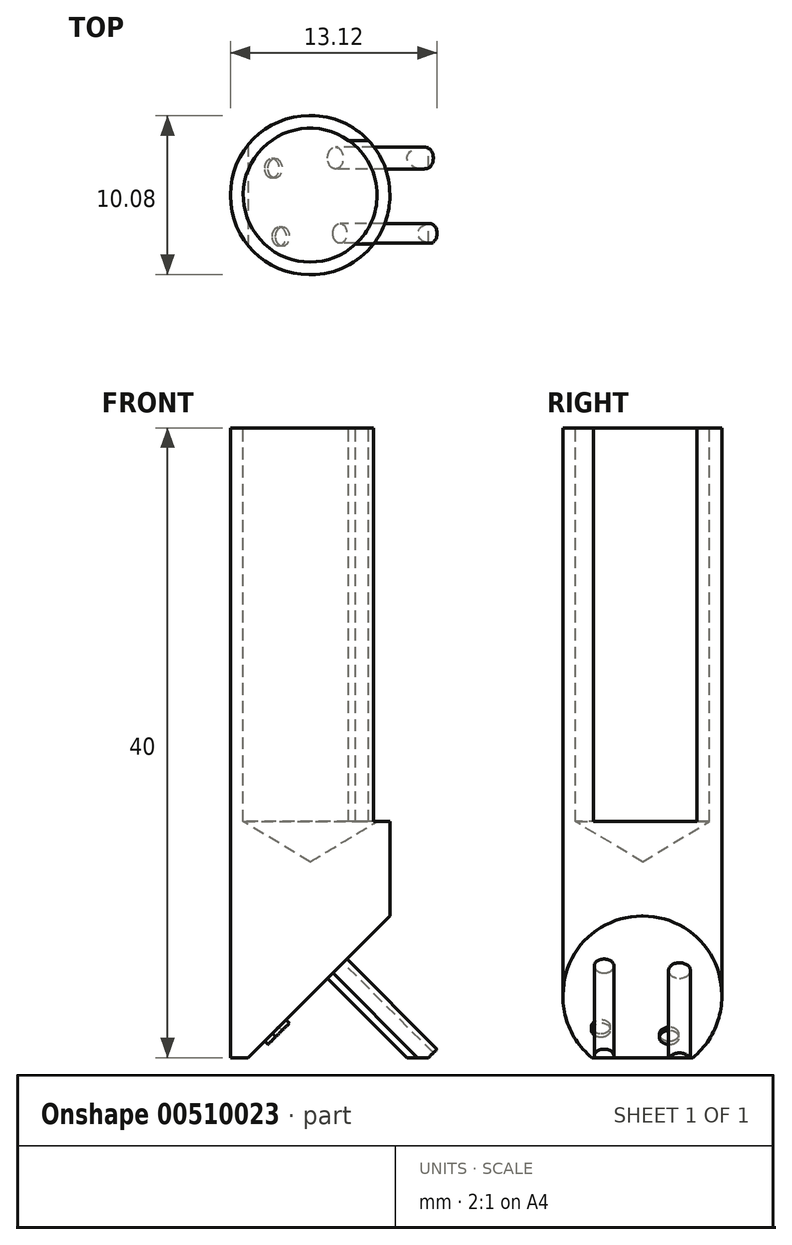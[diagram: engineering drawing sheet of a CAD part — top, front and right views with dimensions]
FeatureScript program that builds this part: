
annotation { "Feature Type Name" : "Feature", "Feature Type Description" : "" }
export const myFeature = defineFeature(function(context is Context, id is Id, definition is map)
    precondition{}
    {
        {
            var Q0;
            Q0=qCreatedBy(makeId("Top.planeOp"),FACE);
            var sketch = newSketch(context, id + "F0", { "sketchPlane" : qUnion([Q0])});
            skLineSegment(sketch, "E0.bottom", {"start": v(-5.06, -5.04) * mm, "end": v(5.06, -5.04) * mm});
            skLineSegment(sketch, "E0.top", {"start": v(-5.06, 5.04) * mm, "end": v(5.06, 5.04) * mm});
            skLineSegment(sketch, "E0.left", {"start": v(-5.06, -5.04) * mm, "end": v(-5.06, 5.04) * mm});
            skLineSegment(sketch, "E0.right", {"start": v(5.06, -5.04) * mm, "end": v(5.06, 5.04) * mm});
            skPoint(sketch, "E0.middle", {"position": v(0, 0) * mm});
            skSolve(sketch);
        }
        {
            var Q0;
            Q0=makeQuery(id+"F0.imprint","IMPRINT",FACE,{"disambiguationData":[TD([[makeQuery(id+"F0.imprint","IMPRINT",EDGE,{"derivedFrom":sQuery(id+"F0.wireOp",EDGE,"E0.bottom")}),1.0]])]});
            extrude(context, id + "F1", {"entities" : qUnion([Q0]), "depth" : 40 * mm});
        }
        {
            var Q0;
            Q0=makeQuery(id+"F1.opExtrude","CAP_FACE",FACE,{"disambiguationData":[OSD([sQuery(id+"F0.wireOp",EDGE,"E0.bottom"),sQuery(id+"F0.wireOp",EDGE,"E0.top"),sQuery(id+"F0.wireOp",EDGE,"E0.left"),sQuery(id+"F0.wireOp",EDGE,"E0.right")])],"isStart":false});
            var sketch = newSketch(context, id + "F2", { "sketchPlane" : qUnion([Q0])});
            skCircle(sketch, "E1", {"center": v(0, 0) * mm, "radius": 3.75 * mm});
            skSolve(sketch);
        }
        {
            var Q0;
            Q0=sQuery(id+"F2.wireOp",VERTEX,"E1.center");
            var Q1;
            Q1=makeQuery(id+"F1.opExtrude","SWEPT_BODY",BODY,{"disambiguationData":[OSD([sQuery(id+"F0.wireOp",EDGE,"E0.bottom"),sQuery(id+"F0.wireOp",EDGE,"E0.top"),sQuery(id+"F0.wireOp",EDGE,"E0.left"),sQuery(id+"F0.wireOp",EDGE,"E0.right")])]});
            hole(context, id + "F3", {"style" : HoleStyle.SIMPLE, "endStyle" : HoleEndStyle.BLIND, "holeDiameter" : 8.5 * mm, "holeDepth" : 25 * mm, "isTappedThrough" : true, "tappedDepth" : 12 * mm, "tapClearance" : 3, "locations" : qUnion([Q0]), "scope" : qUnion([Q1])});
        }
        {
            var Q0;
            Q0=makeQuery(id+"F1.opExtrude","CAP_EDGE",EDGE,{"disambiguationData":[OSD([sQuery(id+"F0.wireOp",EDGE,"E0.right")])],"isStart":true});
            chamfer(context, id + "F4", {"entities" : qUnion([Q0]), "width" : 9 * mm, "tangentPropagation" : true});
        }
        {
            var Q0;
            Q0=makeQuery(id+"F4.opChamfer","BLEND_FACE",FACE,{"disambiguationData":[OSD([sQuery(id+"F0.wireOp",EDGE,"E0.right")])]});
            var sketch = newSketch(context, id + "F5", { "sketchPlane" : qUnion([Q0])});
            skCircle(sketch, "E2", {"center": v(-2.63, 0) * mm, "radius": 0.61 * mm});
            skCircle(sketch, "E3", {"center": v(1.7, -0.67) * mm, "radius": 0.63 * mm});
            skCircle(sketch, "E4", {"center": v(-2.43, 5.46) * mm, "radius": 0.63 * mm});
            skCircle(sketch, "E5", {"center": v(2.36, 5.05) * mm, "radius": 0.7 * mm});
            skSolve(sketch);
        }
        {
            var Q0;
            Q0=makeQuery(id+"F5.imprint","IMPRINT",FACE,{"disambiguationData":[TD([[makeQuery(id+"F5.imprint","IMPRINT",EDGE,{"derivedFrom":sQuery(id+"F5.wireOp",EDGE,"E2")}),1.0]])]});
            var Q1;
            Q1=makeQuery(id+"F5.imprint","IMPRINT",FACE,{"disambiguationData":[TD([[makeQuery(id+"F5.imprint","IMPRINT",EDGE,{"derivedFrom":sQuery(id+"F5.wireOp",EDGE,"E3")}),1.0]])]});
            var Q2;
            Q2=makeQuery(id+"F5.imprint","IMPRINT",FACE,{"disambiguationData":[TD([[makeQuery(id+"F5.imprint","IMPRINT",EDGE,{"derivedFrom":sQuery(id+"F5.wireOp",EDGE,"E5")}),1.0]])]});
            var Q3;
            Q3=makeQuery(id+"F5.imprint","IMPRINT",FACE,{"disambiguationData":[TD([[makeQuery(id+"F5.imprint","IMPRINT",EDGE,{"derivedFrom":sQuery(id+"F5.wireOp",EDGE,"E4")}),1.0]])]});
            extrude(context, id + "F6", {"entities" : qUnion([Q0, Q1, Q2, Q3]), "operationType" : NewBodyOperationType.ADD, "depth" : 0.3 * mm});
        }
        {
            var Q0;
            Q0=makeQuery(id+"F1.opExtrude","CAP_FACE",FACE,{"disambiguationData":[OSD([sQuery(id+"F0.wireOp",EDGE,"E0.bottom"),sQuery(id+"F0.wireOp",EDGE,"E0.top"),sQuery(id+"F0.wireOp",EDGE,"E0.left"),sQuery(id+"F0.wireOp",EDGE,"E0.right")])],"isStart":false});
            var sketch = newSketch(context, id + "F7", { "sketchPlane" : qUnion([Q0])});
            skLineSegment(sketch, "E6.bottom", {"start": v(5.06, -3.11) * mm, "end": v(2.44, -3.11) * mm});
            skLineSegment(sketch, "E6.top", {"start": v(5.06, 3.48) * mm, "end": v(2.44, 3.48) * mm});
            skLineSegment(sketch, "E6.left", {"start": v(5.06, -3.11) * mm, "end": v(5.06, 3.48) * mm});
            skLineSegment(sketch, "E6.right", {"start": v(2.44, -3.11) * mm, "end": v(2.44, 3.48) * mm});
            skSolve(sketch);
        }
        {
            var Q0;
            {var subQ1=sQuery(id+"F7.wireOp",EDGE,"E6.bottom");Q0=makeQuery(id+"F7.imprint","IMPRINT",FACE,{"disambiguationData":[TD([[makeQuery(id+"F7.imprint","IMPRINT",EDGE,{"derivedFrom":subQ1}),-1.0]])]});}
            var Q1;
            {var subQ4=sQuery(id+"F7.wireOp",EDGE,"E6.top");Q1=makeQuery(id+"F7.imprint","IMPRINT",FACE,{"disambiguationData":[TD([[makeQuery(id+"F7.imprint","IMPRINT",EDGE,{"derivedFrom":subQ4}),1.0]])]});}
            extrude(context, id + "F8", {"entities" : qUnion([Q0, Q1]), "operationType" : NewBodyOperationType.REMOVE, "oppositeDirection" : true, "depth" : 25 * mm});
        }
        {
            var Q0;
            Q0=makeQuery(id+"F1.opExtrude","SWEPT_EDGE",EDGE,{"disambiguationData":[OSD([sQuery(id+"F0.wireOp",EDGE,"E0.top"),sQuery(id+"F0.wireOp",EDGE,"E0.left")])]});
            var Q1;
            Q1=makeQuery(id+"F1.opExtrude","SWEPT_EDGE",EDGE,{"disambiguationData":[OSD([sQuery(id+"F0.wireOp",EDGE,"E0.bottom"),sQuery(id+"F0.wireOp",EDGE,"E0.left")])]});
            var Q2;
            Q2=makeQuery(id+"F1.opExtrude","SWEPT_EDGE",EDGE,{"disambiguationData":[OSD([sQuery(id+"F0.wireOp",EDGE,"E0.bottom"),sQuery(id+"F0.wireOp",EDGE,"E0.right")])]});
            var Q3;
            Q3=makeQuery(id+"F1.opExtrude","SWEPT_EDGE",EDGE,{"disambiguationData":[OSD([sQuery(id+"F0.wireOp",EDGE,"E0.top"),sQuery(id+"F0.wireOp",EDGE,"E0.right")])]});
            fillet(context, id + "F9", {"entities" : qUnion([Q0, Q1, Q2, Q3]), "radius" : 5 * mm, "tangentPropagation" : true, "allowEdgeOverflow" : false});
        }
        {
            var Q0;
            Q0=makeQuery(id+"F6.opExtrude","CAP_FACE",FACE,{"disambiguationData":[OSD([sQuery(id+"F5.wireOp",EDGE,"E5")])],"isStart":false});
            var Q1;
            Q1=makeQuery(id+"F6.opExtrude","CAP_FACE",FACE,{"disambiguationData":[OSD([sQuery(id+"F5.wireOp",EDGE,"E4")])],"isStart":false});
            extrude(context, id + "F10", {"entities" : qUnion([Q0, Q1]), "operationType" : NewBodyOperationType.ADD, "depth" : 7.8 * mm});
        }
        {
            var Q0;
            Q0=makeQuery(id+"F1.opExtrude","CAP_FACE",FACE,{"disambiguationData":[OSD([sQuery(id+"F0.wireOp",EDGE,"E0.bottom"),sQuery(id+"F0.wireOp",EDGE,"E0.top"),sQuery(id+"F0.wireOp",EDGE,"E0.left"),sQuery(id+"F0.wireOp",EDGE,"E0.right")])],"isStart":true});
            var sketch = newSketch(context, id + "F11", { "sketchPlane" : qUnion([Q0])});
            skLineSegment(sketch, "E7.bottom", {"start": v(-11.27, 8.85) * mm, "end": v(14.67, 8.85) * mm});
            skLineSegment(sketch, "E7.top", {"start": v(-11.27, -11.73) * mm, "end": v(14.67, -11.73) * mm});
            skLineSegment(sketch, "E7.left", {"start": v(-11.27, 8.85) * mm, "end": v(-11.27, -11.73) * mm});
            skLineSegment(sketch, "E7.right", {"start": v(14.67, 8.85) * mm, "end": v(14.67, -11.73) * mm});
            skSolve(sketch);
        }
        {
            var Q0;
            Q0=makeQuery(id+"F11.imprint","IMPRINT",FACE,{"disambiguationData":[TD([[makeQuery(id+"F11.imprint","IMPRINT",EDGE,{"derivedFrom":sQuery(id+"F11.wireOp",EDGE,"E7.bottom")}),-1.0]])]});
            extrude(context, id + "F12", {"entities" : qUnion([Q0]), "operationType" : NewBodyOperationType.REMOVE, "depth" : 25 * mm});
        }
    });
